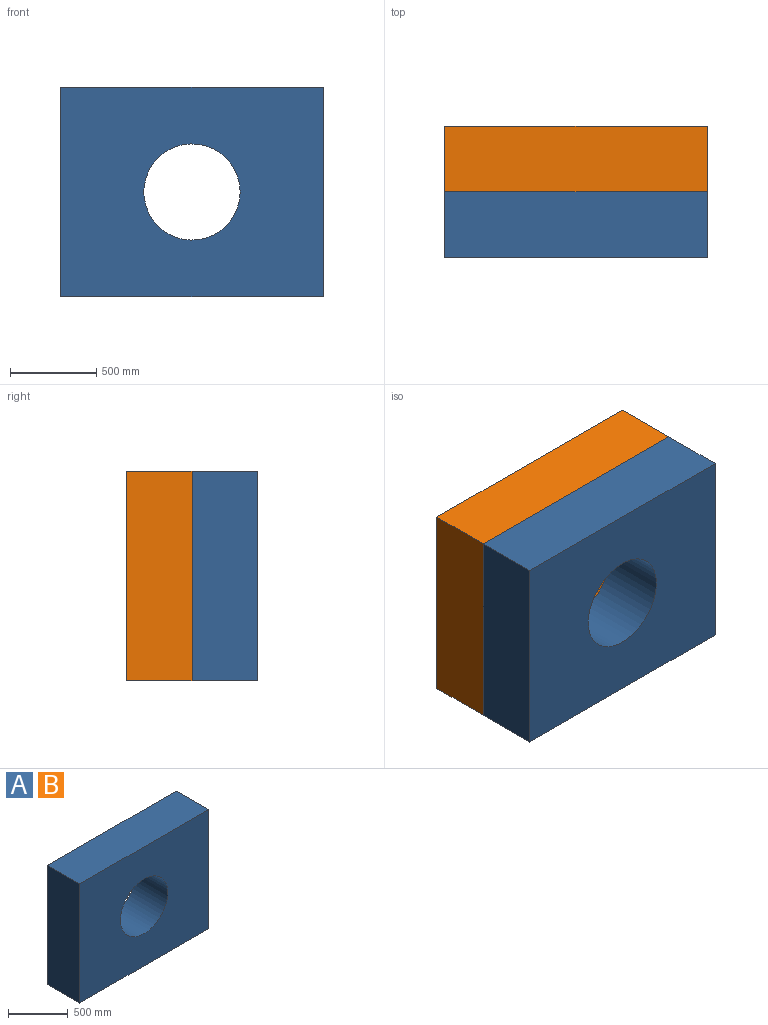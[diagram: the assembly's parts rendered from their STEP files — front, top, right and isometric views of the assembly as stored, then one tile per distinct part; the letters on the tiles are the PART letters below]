
ASSEMBLY  parts=2 mates=1
PART A: 7 faces, bbox 1524x381x1219.2 mm
  f0: plane 1524x381mm, normal (0,0,1), area 580644mm2, adj f1,f4,f5,f6
  f1: plane 1219.2x381mm, normal (-1,0,0), area 464515.2mm2, adj f0,f2,f5,f6
  f2: plane 1524x381mm, normal (0,0,-1), area 580644mm2, adj f1,f4,f5,f6
  f3: cylinder r=279.4mm len=558.8mm, axis (0,1,0), area 668853.9mm2, adj f5,f6
  f4: plane 1219.2x381mm, normal (1,0,0), area 464515.2mm2, adj f0,f2,f5,f6
  f5: plane 1524x1219.2mm, normal (0,-1,0), area 1612814.4mm2, adj f0,f1,f2,f3,f4
  f6: plane 1524x1219.2mm, normal (0,1,0), area 1612814.4mm2, adj f0,f1,f2,f3,f4
PART B: same geometry as A
PLACE A t=(-652.85,53.4,-338.28)mm
PLACE B t=(-652.85,434.4,-338.28)mm
MATE fastened A.f3 <-> B.f3  axis (0,-1,0) through (109.15,-327.6,271.32)mm
